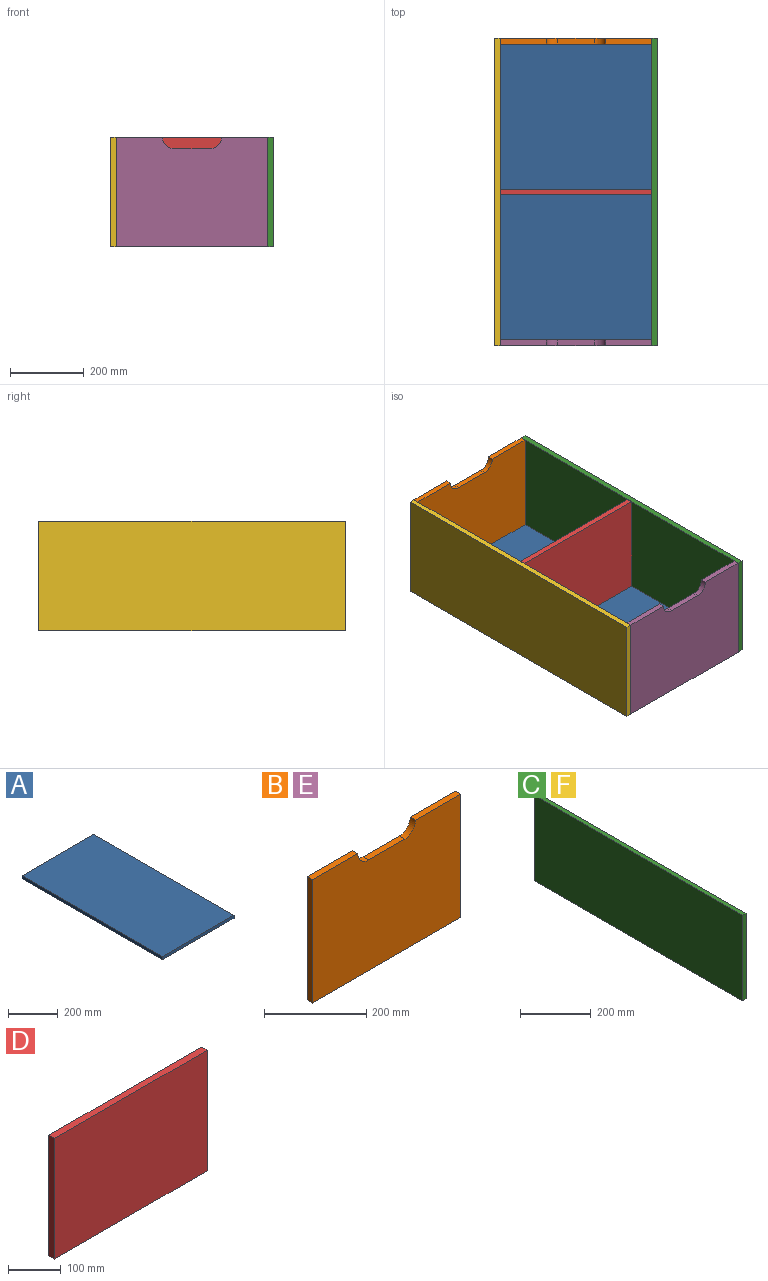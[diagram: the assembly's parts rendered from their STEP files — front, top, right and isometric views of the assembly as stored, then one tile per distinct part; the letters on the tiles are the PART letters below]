
ASSEMBLY  parts=6 mates=5
PART A: 6 faces, bbox 410x800x15 mm
  f0: plane 800x15mm, normal (-1,0,0), area 12000mm2, adj f1,f3,f4,f5
  f1: plane 410x15mm, normal (0,-1,0), area 6150mm2, adj f0,f2,f4,f5
  f2: plane 800x15mm, normal (1,0,0), area 12000mm2, adj f1,f3,f4,f5
  f3: plane 410x15mm, normal (0,1,0), area 6150mm2, adj f0,f2,f4,f5
  f4: plane 800x410mm, normal (0,0,1), area 328000mm2, adj f0,f1,f2,f3
  f5: plane 800x410mm, normal (0,0,-1), area 328000mm2, adj f0,f1,f2,f3
PART B: 10 faces, bbox 410x15x295 mm
  f0: plane 125x15mm, normal (0,0,1), area 1875mm2, adj f1,f2,f6,f8
  f1: plane 410x295mm, normal (0,-1,0), area 116536.3mm2, adj f0,f3,f4,f5,f6,f7,f8,f9
  f2: plane 410x295mm, normal (0,1,0), area 116536.3mm2, adj f0,f3,f4,f5,f6,f7,f8,f9
  f3: plane 410x15mm, normal (0,0,-1), area 6150mm2, adj f1,f2,f4,f6
  f4: plane 295x15mm, normal (1,0,0), area 4425mm2, adj f1,f2,f3,f5
  f5: plane 125x15mm, normal (0,0,1), area 1875mm2, adj f1,f2,f4,f7
  f6: plane 295x15mm, normal (-1,0,0), area 4425mm2, adj f0,f1,f2,f3
  f7: cylinder r=30mm len=30mm, axis (0,-1,0), area 706.9mm2, adj f1,f2,f5,f9
  f8: cylinder r=30mm len=30mm, axis (0,-1,0), area 706.9mm2, adj f0,f1,f2,f9
  f9: plane 100x15mm, normal (0,0,1), area 1500mm2, adj f1,f2,f7,f8
PART C: 6 faces, bbox 15x830x295 mm
  f0: plane 295x15mm, normal (0,-1,0), area 4425mm2, adj f1,f3,f4,f5
  f1: plane 830x15mm, normal (0,0,-1), area 12450mm2, adj f0,f2,f4,f5
  f2: plane 295x15mm, normal (0,1,0), area 4425mm2, adj f1,f3,f4,f5
  f3: plane 830x15mm, normal (0,0,1), area 12450mm2, adj f0,f2,f4,f5
  f4: plane 830x295mm, normal (1,0,0), area 244850mm2, adj f0,f1,f2,f3
  f5: plane 830x295mm, normal (-1,0,0), area 244850mm2, adj f0,f1,f2,f3
PART D: 6 faces, bbox 410x15x280 mm
  f0: plane 280x15mm, normal (-1,0,0), area 4200mm2, adj f1,f3,f4,f5
  f1: plane 410x15mm, normal (0,0,-1), area 6150mm2, adj f0,f2,f4,f5
  f2: plane 280x15mm, normal (1,0,0), area 4200mm2, adj f1,f3,f4,f5
  f3: plane 410x15mm, normal (0,0,1), area 6150mm2, adj f0,f2,f4,f5
  f4: plane 410x280mm, normal (0,-1,0), area 114800mm2, adj f0,f1,f2,f3
  f5: plane 410x280mm, normal (0,1,0), area 114800mm2, adj f0,f1,f2,f3
PART E: same geometry as B
PART F: same geometry as C
PLACE A t=(0,-407.5,-15)mm
PLACE B t=(410,407.5,-15)mm
PLACE C t=(410,-422.5,-15)mm
PLACE D at identity
PLACE E t=(410,-407.5,-15)mm
PLACE F t=(-15,-422.5,-15)mm
MATE fastened A.f4 <-> D.f1  axis (0,0,1) through (205,-7.5,0)mm
MATE fastened C.f5 <-> E.f4  axis (-1,0,0) through (410,-422.5,132.5)mm
MATE fastened A.f1 <-> E.f2  axis (0,-1,0) through (205,-407.5,-15)mm
MATE fastened A.f0 <-> F.f4  axis (-1,0,0) through (0,-407.5,-15)mm
MATE fastened B.f1 <-> A.f3  axis (0,-1,0) through (205,392.5,-15)mm
